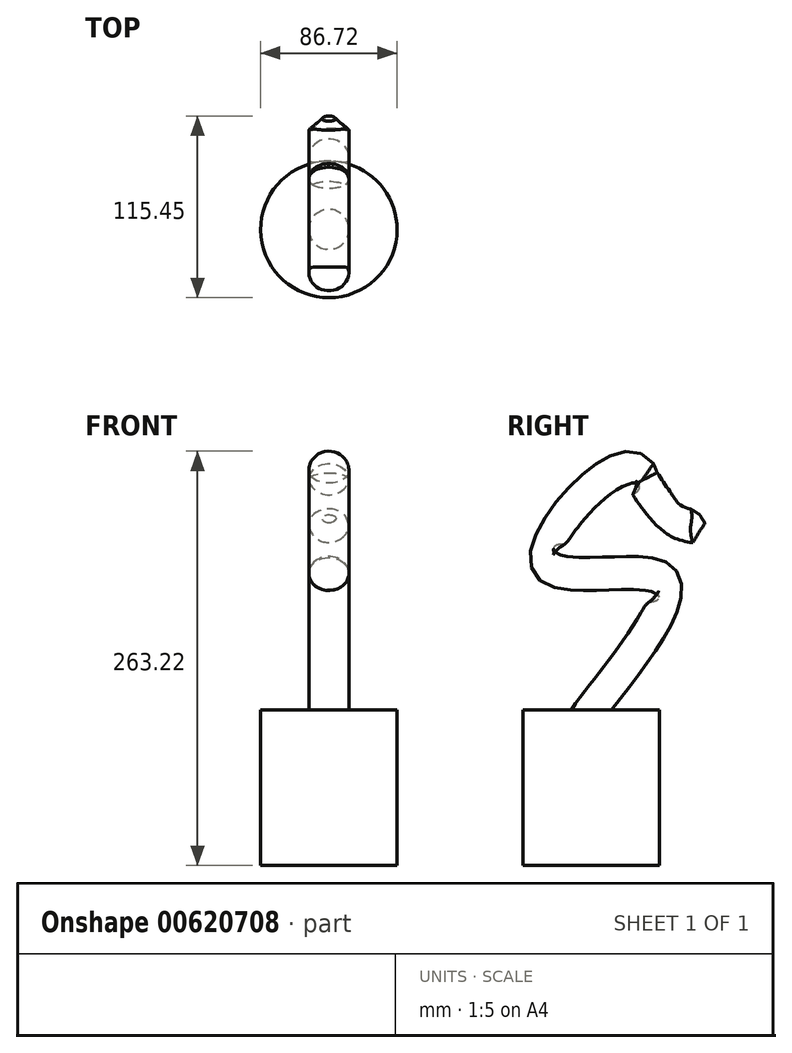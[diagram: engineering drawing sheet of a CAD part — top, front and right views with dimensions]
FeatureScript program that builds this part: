
annotation { "Feature Type Name" : "Feature", "Feature Type Description" : "" }
export const myFeature = defineFeature(function(context is Context, id is Id, definition is map)
    precondition{}
    {
        {
            var Q0;
            Q0=qCreatedBy(makeId("Top.planeOp"),FACE);
            var sketch = newSketch(context, id + "F0", { "sketchPlane" : qUnion([Q0])});
            skCircle(sketch, "E0", {"center": v(0, 0) * mm, "radius": 12.7 * mm});
            skSolve(sketch);
        }
        {
            var Q0;
            Q0=qCreatedBy(makeId("Right.planeOp"),FACE);
            var sketch = newSketch(context, id + "F1", { "sketchPlane" : qUnion([Q0])});
            skFitSpline(sketch, "E1", {"points": [v(0, 0) * mm, v(43.76, 82.22) * mm, v(-27.5, 96.12) * mm, v(32.43, 146.1) * mm], "startDerivative": vector(114.1, 163.1) * mm, "endDerivative": vector(92.63, -237.32) * mm});
            skFitSpline(sketch, "E2", {"points": [v(32.43, 146.1) * mm, v(54.38, 120.97) * mm, v(73.38, 116.75) * mm], "startDerivative": vector(37.24, -54.14) * mm, "endDerivative": vector(45, -2.23) * mm});
            skSolve(sketch);
        }
        {
            var Q0;
            Q0=makeQuery(id+"F0.imprint","IMPRINT",FACE,{"disambiguationData":[TD([[makeQuery(id+"F0.imprint","IMPRINT",EDGE,{"derivedFrom":sQuery(id+"F0.wireOp",EDGE,"E0")}),1.0]])]});
            var Q1;
            Q1=sQuery(id+"F1.wireOp",EDGE,"E2");
            var Q2;
            Q2=sQuery(id+"F1.wireOp",EDGE,"E1");
            sweep(context, id + "F2", {"profiles" : qUnion([Q0]), "path" : qUnion([Q1, Q2])});
        }
        {
            var Q0;
            Q0=qCreatedBy(makeId("Top.planeOp"),FACE);
            var sketch = newSketch(context, id + "F3", { "sketchPlane" : qUnion([Q0])});
            skCircle(sketch, "E3", {"center": v(0, 0) * mm, "radius": 43.36 * mm});
            skSolve(sketch);
        }
        {
            var Q0;
            Q0=makeQuery(id+"F3.imprint","IMPRINT",FACE,{"disambiguationData":[TD([[makeQuery(id+"F3.imprint","IMPRINT",EDGE,{"derivedFrom":sQuery(id+"F3.wireOp",EDGE,"E3")}),1.0]])]});
            extrude(context, id + "F4", {"entities" : qUnion([Q0]), "operationType" : NewBodyOperationType.ADD, "oppositeDirection" : true, "depth" : 98.77 * mm, "offsetDistance" : 25.4 * mm});
        }
        {
            var Q0;
            Q0=makeQuery(id+"F4.opExtrude","CAP_FACE",FACE,{"disambiguationData":[OSD([sQuery(id+"F3.wireOp",EDGE,"E3")])],"isStart":true});
            var sketch = newSketch(context, id + "F5", { "sketchPlane" : qUnion([Q0])});
            skArc(sketch, "E4", {"start": v(43.36, 0) * mm, "mid": v(0, 43.36) * mm, "end": v(-43.36, 0) * mm});
            skSolve(sketch);
        }
        {
            var Q0;
            {var subQ0=sQuery(id+"F5.wireOp",EDGE,"E4");Q0=makeQuery(id+"F5.imprint","IMPRINT",FACE,{"disambiguationData":[TD([[makeQuery(id+"F5.imprint","IMPRINT",EDGE,{"derivedFrom":subQ0}),1.0]])]});}
            var sketch = newSketch(context, id + "F6", { "sketchPlane" : qUnion([Q0])});
            skLineSegment(sketch, "E5", {"start": v(30.11, 0) * mm, "end": v(-29.1, 0) * mm});
            skSolve(sketch);
        }
        {
            var Q0;
            Q0=sQuery(id+"F5.wireOp",EDGE,"E4");
            var Q1;
            Q1=sQuery(id+"F6.wireOp",EDGE,"E5");
            revolve(context, id + "F7", {"bodyType" : ToolBodyType.SURFACE, "surfaceEntities" : qUnion([Q0]), "axis" : qUnion([Q1]), "revolveType" : RevolveType.ONE_DIRECTION, "oppositeDirection" : true, "angle" : 180 * degree});
        }
        {
            var Q0;
            Q0=makeQuery(id+"F2.opSweep","CAP_FACE",FACE,{"disambiguationData":[OSD([sQuery(id+"F0.wireOp",EDGE,"E0"),sQuery(id+"F1.wireOp",VERTEX,"E2.end")])],"isStart":false});
            chamfer(context, id + "F8", {"entities" : qUnion([Q0]), "width" : 8.13 * mm, "tangentPropagation" : true});
        }
    });
